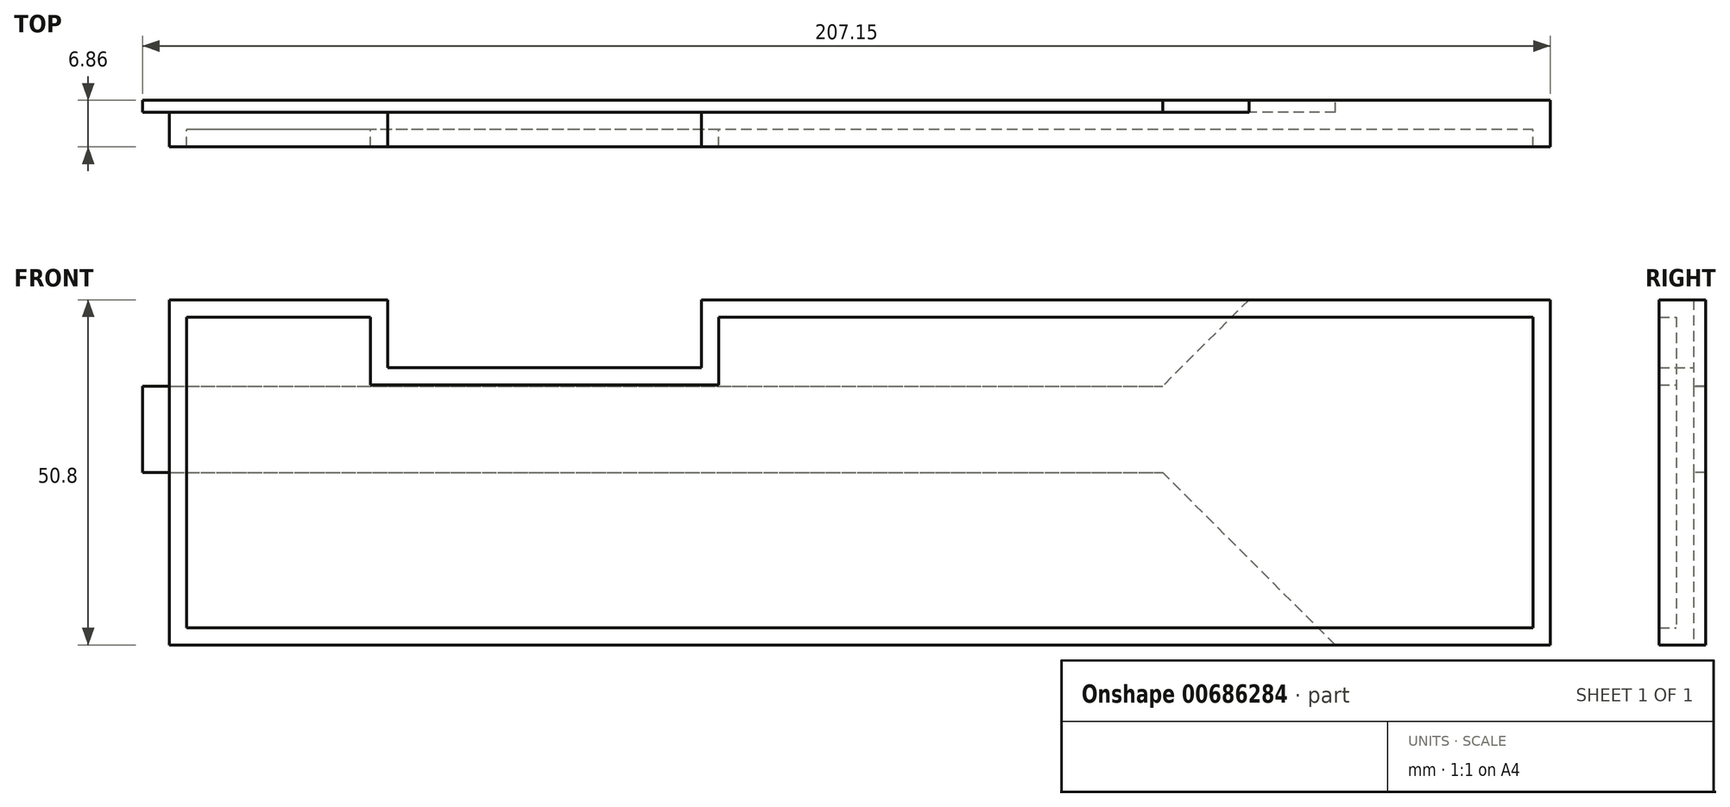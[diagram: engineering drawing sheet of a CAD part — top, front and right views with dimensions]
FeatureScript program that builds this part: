
annotation { "Feature Type Name" : "Feature", "Feature Type Description" : "" }
export const myFeature = defineFeature(function(context is Context, id is Id, definition is map)
    precondition{}
    {
        {
            var Q0;
            Q0=qCreatedBy(makeId("Front.planeOp"),FACE);
            var sketch = newSketch(context, id + "F0", { "sketchPlane" : qUnion([Q0])});
            skLineSegment(sketch, "E0.bottom", {"start": v(104.07, 25.4) * mm, "end": v(-99.13, 25.4) * mm});
            skLineSegment(sketch, "E0.top", {"start": v(104.07, -25.4) * mm, "end": v(-99.13, -25.4) * mm});
            skLineSegment(sketch, "E0.left", {"start": v(104.07, 25.4) * mm, "end": v(104.07, -25.4) * mm});
            skLineSegment(sketch, "E0.right", {"start": v(-99.13, 25.4) * mm, "end": v(-99.13, -25.4) * mm});
            skPoint(sketch, "E0.middle", {"position": v(2.47, 0) * mm});
            skLineSegment(sketch, "E1.bottom", {"start": v(-20.84, 25.4) * mm, "end": v(-67, 25.4) * mm});
            skLineSegment(sketch, "E1.top", {"start": v(-20.84, 15.4) * mm, "end": v(-67, 15.4) * mm});
            skLineSegment(sketch, "E1.left", {"start": v(-20.84, 25.4) * mm, "end": v(-20.84, 15.4) * mm});
            skLineSegment(sketch, "E1.right", {"start": v(-67, 25.4) * mm, "end": v(-67, 15.4) * mm});
            skSolve(sketch);
        }
        {
            var Q0;
            Q0=makeQuery(id+"F0.imprint","IMPRINT",FACE,{"disambiguationData":[TD([[makeQuery(id+"F0.imprint","IMPRINT",EDGE,{"derivedFrom":sQuery(id+"F0.wireOp",EDGE,"E0.bottom")}),1.0]])]});
            extrude(context, id + "F1", {"entities" : qUnion([Q0]), "depth" : 5.08 * mm, "offsetDistance" : 25.4 * mm});
        }
        {
            var Q0;
            Q0=makeQuery(id+"F1.opExtrude","CAP_FACE",FACE,{"disambiguationData":[OSD([sQuery(id+"F0.wireOp",EDGE,"E0.bottom"),sQuery(id+"F0.wireOp",EDGE,"E0.top"),sQuery(id+"F0.wireOp",EDGE,"E0.left"),sQuery(id+"F0.wireOp",EDGE,"E0.right")])],"isStart":false});
            shell(context, id + "F2", {"entities" : qUnion([Q0]), "thickness" : 2.54 * mm});
        }
        {
            var Q0;
            Q0=makeQuery(id+"F1.opExtrude","CAP_FACE",FACE,{"disambiguationData":[OSD([sQuery(id+"F0.wireOp",EDGE,"E0.bottom"),sQuery(id+"F0.wireOp",EDGE,"E0.top"),sQuery(id+"F0.wireOp",EDGE,"E0.left"),sQuery(id+"F0.wireOp",EDGE,"E0.right"),sQuery(id+"F0.wireOp",EDGE,"E1.top"),sQuery(id+"F0.wireOp",EDGE,"E1.left"),sQuery(id+"F0.wireOp",EDGE,"E1.right")])],"isStart":true});
            var sketch = newSketch(context, id + "F3", { "sketchPlane" : qUnion([Q0])});
            skLineSegment(sketch, "E2.bottom", {"start": v(103.08, 12.67) * mm, "end": v(-47, 12.67) * mm});
            skLineSegment(sketch, "E2.top", {"start": v(103.08, 0) * mm, "end": v(-47, 0) * mm});
            skLineSegment(sketch, "E2.left", {"start": v(103.08, 12.67) * mm, "end": v(103.08, 0) * mm});
            skLineSegment(sketch, "E2.right", {"start": v(-47, 12.67) * mm, "end": v(-47, 0) * mm});
            skSolve(sketch);
        }
        {
            var Q0;
            Q0=makeQuery(id+"F3.imprint","IMPRINT",FACE,{"disambiguationData":[TD([[makeQuery(id+"F3.imprint","IMPRINT",EDGE,{"derivedFrom":sQuery(id+"F3.wireOp",EDGE,"E2.bottom")}),1.0]])]});
            extrude(context, id + "F4", {"entities" : qUnion([Q0]), "operationType" : NewBodyOperationType.ADD, "depth" : 1.78 * mm, "offsetDistance" : 25.4 * mm});
        }
        {
            var Q0;
            Q0=makeQuery(id+"F1.opExtrude","CAP_FACE",FACE,{"disambiguationData":[OSD([sQuery(id+"F0.wireOp",EDGE,"E0.bottom"),sQuery(id+"F0.wireOp",EDGE,"E0.top"),sQuery(id+"F0.wireOp",EDGE,"E0.left"),sQuery(id+"F0.wireOp",EDGE,"E0.right"),sQuery(id+"F0.wireOp",EDGE,"E1.top"),sQuery(id+"F0.wireOp",EDGE,"E1.left"),sQuery(id+"F0.wireOp",EDGE,"E1.right")])],"isStart":true});
            var sketch = newSketch(context, id + "F5", { "sketchPlane" : qUnion([Q0])});
            skLineSegment(sketch, "E3.bottom", {"start": v(-47, 25.4) * mm, "end": v(-104.07, 25.4) * mm});
            skLineSegment(sketch, "E3.top", {"start": v(-47, -25.4) * mm, "end": v(-104.07, -25.4) * mm});
            skLineSegment(sketch, "E3.left", {"start": v(-47, 25.4) * mm, "end": v(-47, -25.4) * mm});
            skLineSegment(sketch, "E3.right", {"start": v(-104.07, 25.4) * mm, "end": v(-104.07, -25.4) * mm});
            skSolve(sketch);
        }
        {
            var Q0;
            {var subQ3=sQuery(id+"F5.wireOp",EDGE,"E3.bottom");Q0=makeQuery(id+"F5.imprint","IMPRINT",FACE,{"disambiguationData":[TD([[makeQuery(id+"F5.imprint","IMPRINT",EDGE,{"derivedFrom":subQ3}),-1.0]])]});}
            extrude(context, id + "F6", {"entities" : qUnion([Q0]), "operationType" : NewBodyOperationType.ADD, "depth" : 1.78 * mm, "offsetDistance" : 25.4 * mm});
        }
        {
            var Q0;
            Q0=makeQuery(id+"F6.opExtrude","SWEPT_EDGE",EDGE,{"disambiguationData":[OSD([sQuery(id+"F0.wireOp",EDGE,"E0.bottom"),sQuery(id+"F5.wireOp",EDGE,"E3.bottom"),sQuery(id+"F5.wireOp",EDGE,"E3.left")])]});
            chamfer(context, id + "F7", {"entities" : qUnion([Q0]), "width" : 12.7 * mm, "tangentPropagation" : true});
        }
        {
            var Q0;
            Q0=makeQuery(id+"F6.opExtrude","SWEPT_EDGE",EDGE,{"disambiguationData":[OSD([sQuery(id+"F0.wireOp",EDGE,"E0.top"),sQuery(id+"F5.wireOp",EDGE,"E3.top"),sQuery(id+"F5.wireOp",EDGE,"E3.left")])]});
            chamfer(context, id + "F8", {"entities" : qUnion([Q0]), "width" : 25.4 * mm, "tangentPropagation" : true});
        }
    });
